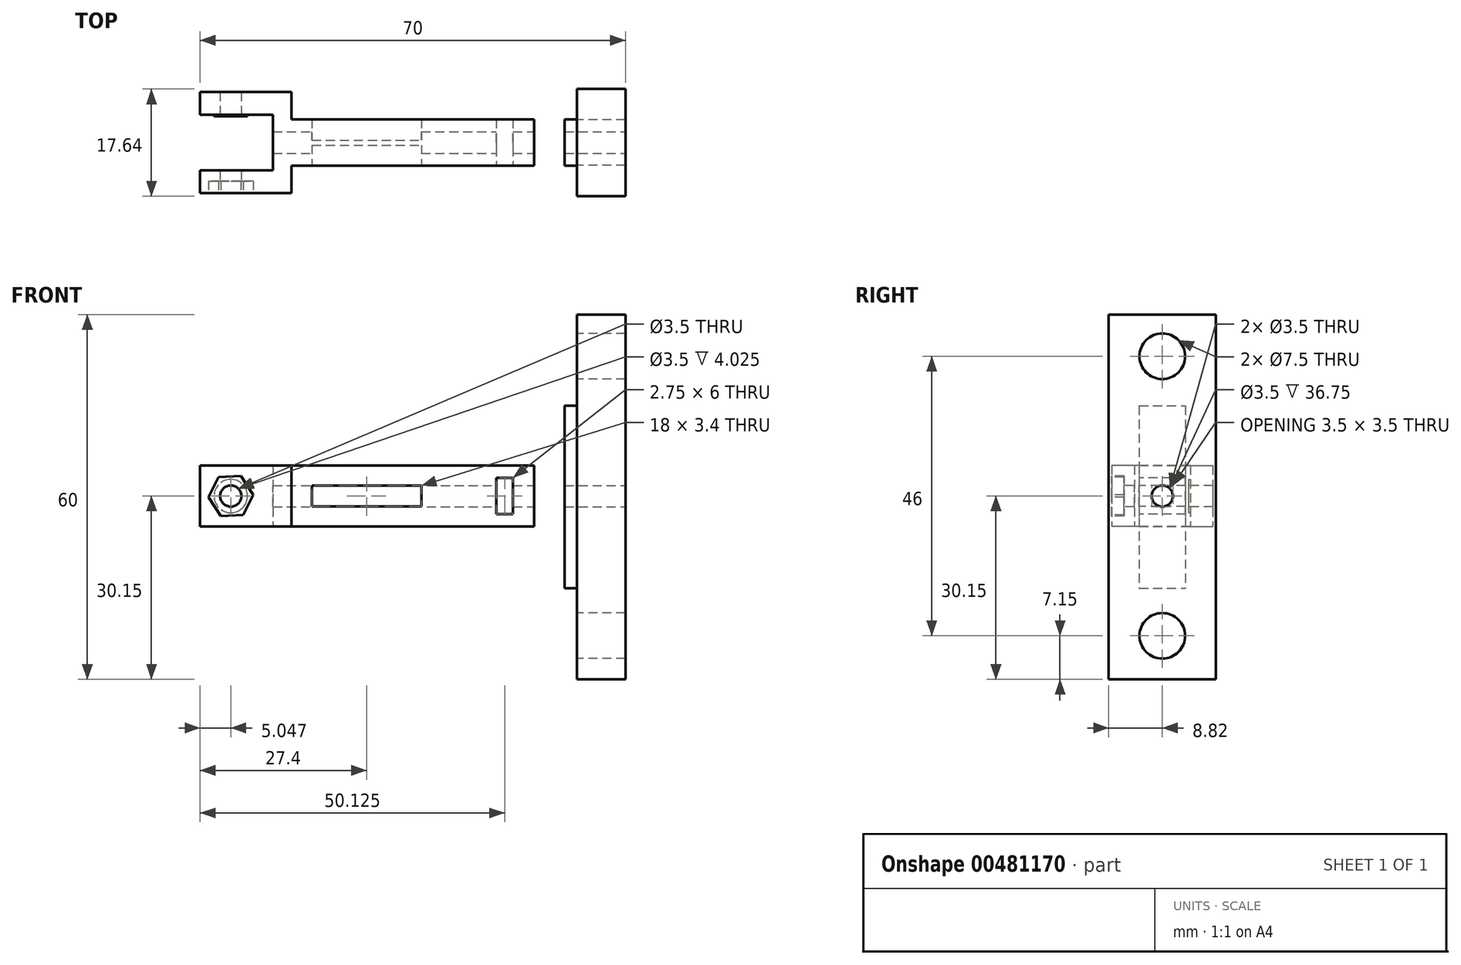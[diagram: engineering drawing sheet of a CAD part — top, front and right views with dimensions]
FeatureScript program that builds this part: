
annotation { "Feature Type Name" : "Feature", "Feature Type Description" : "" }
export const myFeature = defineFeature(function(context is Context, id is Id, definition is map)
    precondition{}
    {
        {
            var Q0;
            Q0=qCreatedBy(makeId("Top.planeOp"),FACE);
            var sketch = newSketch(context, id + "F0", { "sketchPlane" : qUnion([Q0])});
            skLineSegment(sketch, "E0.bottom", {"start": v(0, 0) * mm, "end": v(40, 0) * mm});
            skLineSegment(sketch, "E0.top", {"start": v(0, -3.83) * mm, "end": v(40, -3.83) * mm});
            skLineSegment(sketch, "E0.left", {"start": v(0, 0) * mm, "end": v(0, -3.83) * mm});
            skLineSegment(sketch, "E0.right", {"start": v(40, 0) * mm, "end": v(40, -3.83) * mm});
            skLineSegment(sketch, "E1.bottom", {"start": v(-3, 0) * mm, "end": v(0, 0) * mm});
            skLineSegment(sketch, "E1.top", {"start": v(-15, -8.32) * mm, "end": v(0, -8.32) * mm});
            skLineSegment(sketch, "E1.left", {"start": v(-15, -4.6) * mm, "end": v(-15, -8.32) * mm});
            skLineSegment(sketch, "E1.right", {"start": v(0, 0) * mm, "end": v(0, -8.32) * mm});
            skLineSegment(sketch, "E2.top", {"start": v(-15, -4.6) * mm, "end": v(-3, -4.6) * mm});
            skLineSegment(sketch, "E2.right", {"start": v(-3, 0) * mm, "end": v(-3, -4.6) * mm});
            skLineSegment(sketch, "E3.MirrorCS", {"start": v(0, 0) * mm, "end": v(0, 3.83) * mm});
            skLineSegment(sketch, "E4.MirrorCS", {"start": v(0, 0) * mm, "end": v(0, 8.32) * mm});
            skLineSegment(sketch, "E5.MirrorCS", {"start": v(-15, 4.6) * mm, "end": v(-15, 8.32) * mm});
            skLineSegment(sketch, "E6.MirrorCS", {"start": v(-3, 0) * mm, "end": v(-3, 4.6) * mm});
            skLineSegment(sketch, "E7.MirrorCS", {"start": v(-15, 8.32) * mm, "end": v(0, 8.32) * mm});
            skLineSegment(sketch, "E8.MirrorCS", {"start": v(-15, 4.6) * mm, "end": v(-3, 4.6) * mm});
            skLineSegment(sketch, "E9.MirrorCS", {"start": v(40, 0) * mm, "end": v(40, 3.83) * mm});
            skLineSegment(sketch, "E10.MirrorCS", {"start": v(0, 3.83) * mm, "end": v(40, 3.83) * mm});
            skSolve(sketch);
        }
        {
            var Q0;
            {var subQ2=sQuery(id+"F0.wireOp",EDGE,"E1.top");Q0=makeQuery(id+"F0.imprint","IMPRINT",FACE,{"disambiguationData":[TD([[makeQuery(id+"F0.imprint","IMPRINT",EDGE,{"derivedFrom":subQ2}),1.0]])]});}
            var Q1;
            Q1=makeQuery(id+"F0.imprint","IMPRINT",FACE,{"disambiguationData":[TD([[makeQuery(id+"F0.imprint","IMPRINT",EDGE,{"derivedFrom":sQuery(id+"F0.wireOp",EDGE,"E5.MirrorCS")}),-1.0]])]});
            var Q2;
            {var subQ0=sQuery(id+"F0.wireOp",EDGE,"E0.bottom");Q2=makeQuery(id+"F0.imprint","IMPRINT",FACE,{"disambiguationData":[TD([[makeQuery(id+"F0.imprint","IMPRINT",EDGE,{"derivedFrom":subQ0}),1.0]])]});}
            var Q3;
            {var subQ0=sQuery(id+"F0.wireOp",EDGE,"E0.bottom");Q3=makeQuery(id+"F0.imprint","IMPRINT",FACE,{"disambiguationData":[TD([[makeQuery(id+"F0.imprint","IMPRINT",EDGE,{"derivedFrom":subQ0}),-1.0]])]});}
            extrude(context, id + "F1", {"entities" : qUnion([Q0, Q1, Q2, Q3]), "depth" : 10 * mm});
        }
        {
            var Q0;
            Q0=makeQuery(id+"F1.opExtrude","SWEPT_FACE",FACE,{"disambiguationData":[OSD([sQuery(id+"F0.wireOp",EDGE,"E1.top")])]});
            var sketch = newSketch(context, id + "F2", { "sketchPlane" : qUnion([Q0])});
            skCircle(sketch, "E11", {"center": v(-9.95, 5) * mm, "radius": 1.75 * mm});
            skSolve(sketch);
        }
        {
            var Q0;
            Q0=makeQuery(id+"F2.imprint","IMPRINT",FACE,{"disambiguationData":[TD([[makeQuery(id+"F2.imprint","IMPRINT",EDGE,{"derivedFrom":sQuery(id+"F2.wireOp",EDGE,"E11")}),1.0]])]});
            extrude(context, id + "F3", {"entities" : qUnion([Q0]), "operationType" : NewBodyOperationType.REMOVE, "endBound" : BoundingType.THROUGH_ALL, "oppositeDirection" : true, "depth" : 25 * mm});
        }
        {
            var Q0;
            Q0=makeQuery(id+"F1.opExtrude","SWEPT_FACE",FACE,{"disambiguationData":[OSD([sQuery(id+"F0.wireOp",EDGE,"E0.top")])]});
            var sketch = newSketch(context, id + "F4", { "sketchPlane" : qUnion([Q0])});
            skLineSegment(sketch, "E12.bottom", {"start": v(3.4, 3.3) * mm, "end": v(21.4, 3.3) * mm});
            skLineSegment(sketch, "E12.top", {"start": v(3.4, 6.7) * mm, "end": v(21.4, 6.7) * mm});
            skLineSegment(sketch, "E12.left", {"start": v(3.4, 3.3) * mm, "end": v(3.4, 6.7) * mm});
            skLineSegment(sketch, "E12.right", {"start": v(21.4, 3.3) * mm, "end": v(21.4, 6.7) * mm});
            skLineSegment(sketch, "E13.bottom", {"start": v(33.75, 8) * mm, "end": v(36.5, 8) * mm});
            skLineSegment(sketch, "E13.top", {"start": v(33.75, 2) * mm, "end": v(36.5, 2) * mm});
            skLineSegment(sketch, "E13.left", {"start": v(33.75, 8) * mm, "end": v(33.75, 2) * mm});
            skLineSegment(sketch, "E13.right", {"start": v(36.5, 8) * mm, "end": v(36.5, 2) * mm});
            skSolve(sketch);
        }
        {
            var Q0;
            Q0=makeQuery(id+"F4.imprint","IMPRINT",FACE,{"disambiguationData":[TD([[makeQuery(id+"F4.imprint","IMPRINT",EDGE,{"derivedFrom":sQuery(id+"F4.wireOp",EDGE,"E12.bottom")}),1.0]])]});
            var Q1;
            Q1=makeQuery(id+"F4.imprint","IMPRINT",FACE,{"disambiguationData":[TD([[makeQuery(id+"F4.imprint","IMPRINT",EDGE,{"derivedFrom":sQuery(id+"F4.wireOp",EDGE,"E13.bottom")}),-1.0]])]});
            extrude(context, id + "F5", {"entities" : qUnion([Q0, Q1]), "operationType" : NewBodyOperationType.REMOVE, "endBound" : BoundingType.THROUGH_ALL, "oppositeDirection" : true, "depth" : 25 * mm});
        }
        {
            var Q0;
            Q0=makeQuery(id+"F1.opExtrude","SWEPT_FACE",FACE,{"disambiguationData":[OSD([sQuery(id+"F0.wireOp",EDGE,"E0.right"),sQuery(id+"F0.wireOp",EDGE,"E9.MirrorCS")])]});
            var sketch = newSketch(context, id + "F6", { "sketchPlane" : qUnion([Q0])});
            skCircle(sketch, "E14", {"center": v(0, 5) * mm, "radius": 1.75 * mm});
            skSolve(sketch);
        }
        {
            var Q0;
            Q0=makeQuery(id+"F6.imprint","IMPRINT",FACE,{"disambiguationData":[TD([[makeQuery(id+"F6.imprint","IMPRINT",EDGE,{"derivedFrom":sQuery(id+"F6.wireOp",EDGE,"E14")}),1.0]])]});
            extrude(context, id + "F7", {"entities" : qUnion([Q0]), "operationType" : NewBodyOperationType.REMOVE, "oppositeDirection" : true, "depth" : 15 * mm});
        }
        {
            var Q0;
            Q0=makeQuery(id+"F1.opExtrude","SWEPT_FACE",FACE,{"disambiguationData":[OSD([sQuery(id+"F0.wireOp",EDGE,"E0.right"),sQuery(id+"F0.wireOp",EDGE,"E9.MirrorCS")])]});
            cPlane(context, id + "F8", {"entities" : qUnion([Q0]), "cplaneType" : CPlaneType.OFFSET, "offset" : 5 * mm, "width" : 150 * mm, "height" : 150 * mm});
        }
        {
            var Q0;
            Q0=qCreatedBy(id+"F8.planeOp",FACE);
            var sketch = newSketch(context, id + "F9", { "sketchPlane" : qUnion([Q0])});
            skLineSegment(sketch, "E15.0", {"start": v(3.83, 10) * mm, "end": v(3.83, 0) * mm});
            skLineSegment(sketch, "E16.0", {"start": v(-3.82, 10) * mm, "end": v(-3.82, 0) * mm});
            skLineSegment(sketch, "E17.bottom", {"start": v(-3.82, 19.85) * mm, "end": v(3.83, 19.85) * mm});
            skLineSegment(sketch, "E17.top", {"start": v(-3.82, -10.15) * mm, "end": v(3.83, -10.15) * mm});
            skLineSegment(sketch, "E17.left", {"start": v(-3.82, 19.85) * mm, "end": v(-3.82, -10.15) * mm});
            skLineSegment(sketch, "E17.right", {"start": v(3.83, 19.85) * mm, "end": v(3.83, -10.15) * mm});
            skPoint(sketch, "E18.oppositeSnap0", {"position": v(3.83, 4.85) * mm});
            skLineSegment(sketch, "E18.bottom", {"start": v(3.83, 4.85) * mm, "end": v(3.83, 4.85) * mm});
            skLineSegment(sketch, "E18.top", {"start": v(3.83, 4.85) * mm, "end": v(3.83, 4.85) * mm});
            skLineSegment(sketch, "E18.left", {"start": v(3.83, 4.85) * mm, "end": v(3.83, 4.85) * mm});
            skLineSegment(sketch, "E18.right", {"start": v(3.83, 4.85) * mm, "end": v(3.83, 4.85) * mm});
            skSolve(sketch);
        }
        {
            var Q0;
            {var subQ0=sQuery(id+"F9.wireOp",EDGE,"E17.bottom");Q0=makeQuery(id+"F9.imprint","IMPRINT",FACE,{"disambiguationData":[TD([[makeQuery(id+"F9.imprint","IMPRINT",EDGE,{"derivedFrom":subQ0}),-1.0]])]});}
            extrude(context, id + "F10", {"entities" : qUnion([Q0]), "depth" : 2 * mm});
        }
        {
            var Q0;
            Q0=makeQuery(id+"F10.opExtrude","CAP_FACE",FACE,{"disambiguationData":[OSD([sQuery(id+"F9.wireOp",EDGE,"E17.bottom"),sQuery(id+"F9.wireOp",EDGE,"E17.top"),sQuery(id+"F9.wireOp",EDGE,"E17.left"),sQuery(id+"F9.wireOp",EDGE,"E17.right")])],"isStart":false});
            var sketch = newSketch(context, id + "F11", { "sketchPlane" : qUnion([Q0])});
            skLineSegment(sketch, "E19.bottom", {"start": v(8.82, 34.85) * mm, "end": v(-8.83, 34.85) * mm});
            skLineSegment(sketch, "E19.top", {"start": v(8.83, -25.15) * mm, "end": v(-8.82, -25.15) * mm});
            skLineSegment(sketch, "E19.left", {"start": v(8.82, 34.85) * mm, "end": v(8.83, -25.15) * mm});
            skLineSegment(sketch, "E19.right", {"start": v(-8.83, 34.85) * mm, "end": v(-8.82, -25.15) * mm});
            skSolve(sketch);
        }
        {
            var Q0;
            Q0=qSketchRegion(id+"F11",true);
            extrude(context, id + "F12", {"entities" : qUnion([Q0]), "operationType" : NewBodyOperationType.ADD, "depth" : 8 * mm});
        }
        {
            var Q0;
            Q0=makeQuery(id+"F12.opExtrude","CAP_FACE",FACE,{"disambiguationData":[OSD([sQuery(id+"F11.wireOp",EDGE,"E19.bottom"),sQuery(id+"F11.wireOp",EDGE,"E19.top"),sQuery(id+"F11.wireOp",EDGE,"E19.left"),sQuery(id+"F11.wireOp",EDGE,"E19.right")])],"isStart":false});
            var sketch = newSketch(context, id + "F13", { "sketchPlane" : qUnion([Q0])});
            skCircle(sketch, "E20.0", {"center": v(0, 5) * mm, "radius": 1.75 * mm});
            skSolve(sketch);
        }
        {
            var Q0;
            Q0=makeQuery(id+"F13.imprint","IMPRINT",FACE,{"disambiguationData":[TD([[makeQuery(id+"F13.imprint","IMPRINT",EDGE,{"derivedFrom":sQuery(id+"F13.wireOp",EDGE,"E20.0")}),1.0]])]});
            extrude(context, id + "F14", {"entities" : qUnion([Q0]), "operationType" : NewBodyOperationType.REMOVE, "endBound" : BoundingType.THROUGH_ALL, "oppositeDirection" : true, "depth" : 25 * mm});
        }
        {
            var Q0;
            Q0=makeQuery(id+"F1.opExtrude","SWEPT_FACE",FACE,{"disambiguationData":[OSD([sQuery(id+"F0.wireOp",EDGE,"E8.MirrorCS")])]});
            var sketch = newSketch(context, id + "F15", { "sketchPlane" : qUnion([Q0])});
            skCircle(sketch, "E21", {"center": v(-9.95, 5) * mm, "radius": 1.75 * mm});
            skCircle(sketch, "E22", {"center": v(-9.95, 5) * mm, "radius": 2.75 * mm});
            skSolve(sketch);
        }
        {
            var Q0;
            Q0=makeQuery(id+"F15.imprint","IMPRINT",FACE,{"disambiguationData":[TD([[makeQuery(id+"F15.imprint","IMPRINT",EDGE,{"derivedFrom":sQuery(id+"F15.wireOp",EDGE,"E21")}),1.0]])]});
            extrude(context, id + "F16", {"entities" : qUnion([Q0]), "operationType" : NewBodyOperationType.ADD, "depth" : 0.3 * mm});
        }
        {
            var Q0;
            Q0=makeQuery(id+"F1.opExtrude","SWEPT_FACE",FACE,{"disambiguationData":[OSD([sQuery(id+"F0.wireOp",EDGE,"E1.top")])]});
            var sketch = newSketch(context, id + "F17", { "sketchPlane" : qUnion([Q0])});
            skCircle(sketch, "E23.cCircle", {"center": v(-9.95, 5) * mm, "radius": 3.2 * mm, "construction": true});
            skLineSegment(sketch, "E23.0", {"start": v(-6.26, 5.2) * mm, "end": v(-7.93, 1.9) * mm});
            skLineSegment(sketch, "E23.1", {"start": v(-7.93, 1.9) * mm, "end": v(-11.62, 1.7) * mm});
            skLineSegment(sketch, "E23.2", {"start": v(-11.62, 1.7) * mm, "end": v(-13.64, 4.8) * mm});
            skLineSegment(sketch, "E23.3", {"start": v(-13.64, 4.8) * mm, "end": v(-11.98, 8.1) * mm});
            skLineSegment(sketch, "E23.4", {"start": v(-11.98, 8.1) * mm, "end": v(-8.29, 8.3) * mm});
            skLineSegment(sketch, "E23.5", {"start": v(-8.29, 8.3) * mm, "end": v(-6.26, 5.2) * mm});
            skPoint(sketch, "E23.0.midPoint", {"position": v(-7.1, 3.56) * mm});
            skSolve(sketch);
        }
        {
            var Q0;
            Q0=makeQuery(id+"F17.imprint","IMPRINT",FACE,{"disambiguationData":[TD([[makeQuery(id+"F17.imprint","IMPRINT",EDGE,{"derivedFrom":sQuery(id+"F17.wireOp",EDGE,"E23.0")}),-1.0]])]});
            extrude(context, id + "F18", {"entities" : qUnion([Q0]), "operationType" : NewBodyOperationType.REMOVE, "oppositeDirection" : true, "depth" : 2 * mm});
        }
        {
            var Q0;
            Q0=makeQuery(id+"F12.opExtrude","CAP_FACE",FACE,{"disambiguationData":[OSD([sQuery(id+"F11.wireOp",EDGE,"E19.bottom"),sQuery(id+"F11.wireOp",EDGE,"E19.top"),sQuery(id+"F11.wireOp",EDGE,"E19.left"),sQuery(id+"F11.wireOp",EDGE,"E19.right")])],"isStart":true});
            var sketch = newSketch(context, id + "F19", { "sketchPlane" : qUnion([Q0])});
            skCircle(sketch, "E24.0", {"center": v(0, 5) * mm, "radius": 1.75 * mm});
            skCircle(sketch, "E25", {"center": v(0, -18) * mm, "radius": 3.75 * mm});
            skCircle(sketch, "E26", {"center": v(0, 28) * mm, "radius": 3.75 * mm});
            skSolve(sketch);
        }
        {
            var Q0;
            Q0=sQuery(id+"F19.wireOp",VERTEX,"E25.center");
            var Q1;
            Q1=sQuery(id+"F19.wireOp",VERTEX,"E26.center");
            var Q2;
            Q2=makeQuery(id+"F10.opExtrude","SWEPT_BODY",BODY,{"disambiguationData":[OSD([sQuery(id+"F9.wireOp",EDGE,"E17.bottom"),sQuery(id+"F9.wireOp",EDGE,"E17.top"),sQuery(id+"F9.wireOp",EDGE,"E17.left"),sQuery(id+"F9.wireOp",EDGE,"E17.right")])]});
            hole(context, id + "F20", {"style" : HoleStyle.SIMPLE, "endStyle" : HoleEndStyle.THROUGH, "holeDiameter" : 7.5 * mm, "isTappedThrough" : true, "tappedDepth" : 12 * mm, "tapClearance" : 3, "locations" : qUnion([Q0, Q1]), "scope" : qUnion([Q2])});
        }
    });
